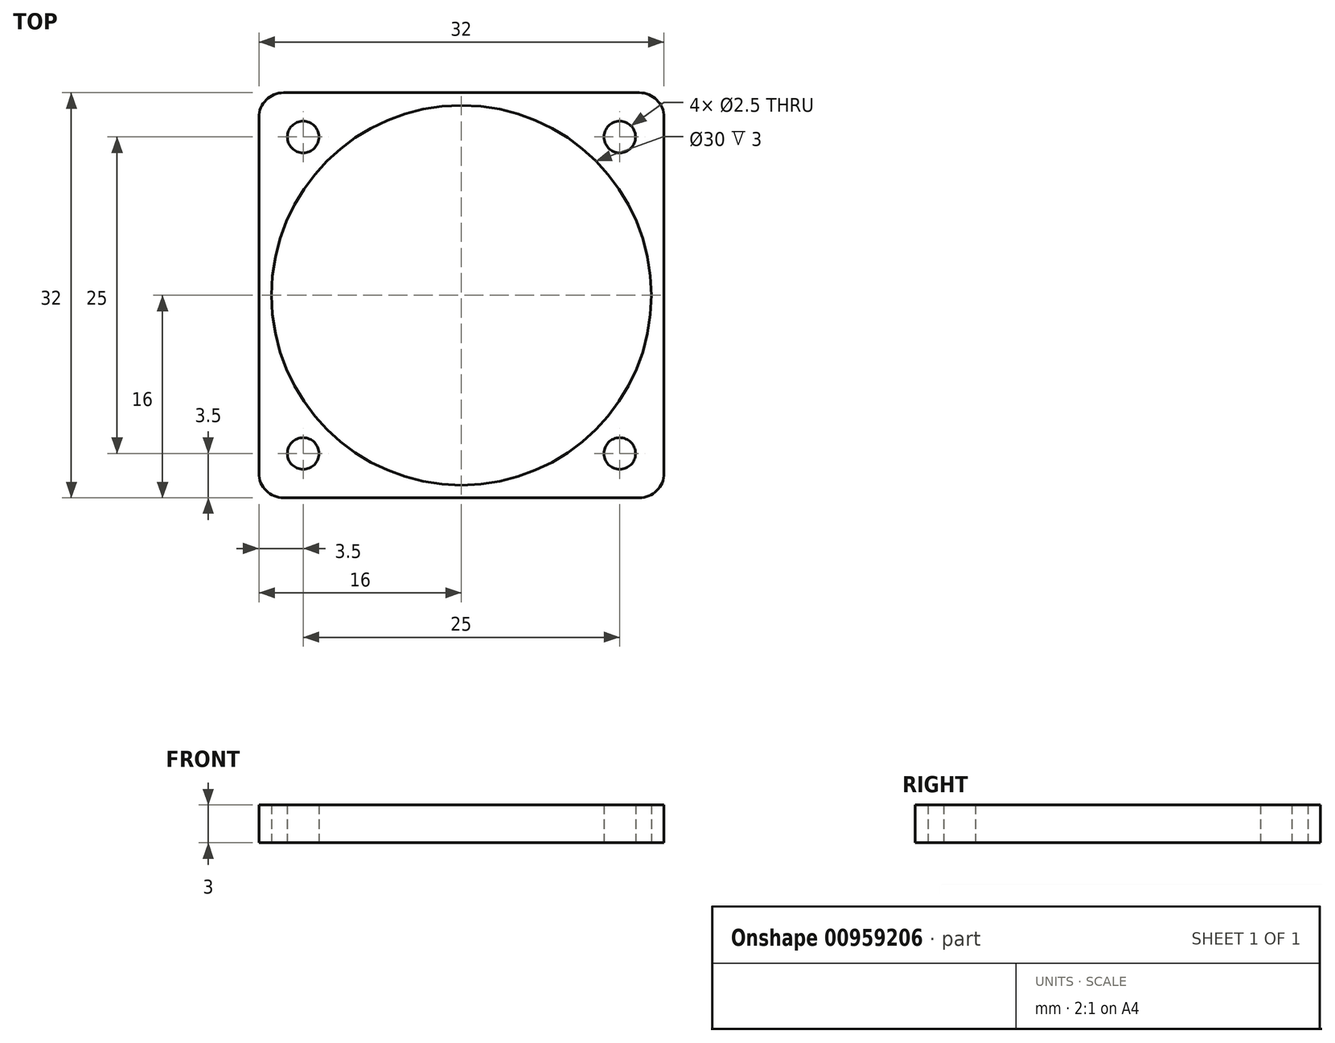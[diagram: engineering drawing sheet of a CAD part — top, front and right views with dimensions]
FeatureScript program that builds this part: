
annotation { "Feature Type Name" : "Feature", "Feature Type Description" : "" }
export const myFeature = defineFeature(function(context is Context, id is Id, definition is map)
    precondition{}
    {
        {
            var Q0;
            Q0=qCreatedBy(makeId("Top.planeOp"),FACE);
            var sketch = newSketch(context, id + "F0", { "sketchPlane" : qUnion([Q0])});
            skCircle(sketch, "E0", {"center": v(0, 0) * mm, "radius": 15 * mm});
            skCircle(sketch, "E1", {"center": v(0, 0) * mm, "radius": 17.68 * mm, "construction": true});
            skLineSegment(sketch, "E2.bottom", {"start": v(16, -16) * mm, "end": v(-16, -16) * mm});
            skLineSegment(sketch, "E2.top", {"start": v(16, 16) * mm, "end": v(-16, 16) * mm});
            skLineSegment(sketch, "E2.left", {"start": v(16, -16) * mm, "end": v(16, 16) * mm});
            skLineSegment(sketch, "E2.right", {"start": v(-16, -16) * mm, "end": v(-16, 16) * mm});
            skLineSegment(sketch, "E3", {"start": v(-16, 16) * mm, "end": v(16, -16) * mm, "construction": true});
            skLineSegment(sketch, "E4", {"start": v(-16, -16) * mm, "end": v(16, 16) * mm, "construction": true});
            skCircle(sketch, "E5", {"center": v(-12.5, 12.5) * mm, "radius": 1.25 * mm});
            skCircle(sketch, "E6", {"center": v(12.5, 12.5) * mm, "radius": 1.25 * mm});
            skCircle(sketch, "E7", {"center": v(-12.5, -12.5) * mm, "radius": 1.25 * mm});
            skCircle(sketch, "E8", {"center": v(12.5, -12.5) * mm, "radius": 1.25 * mm});
            skSolve(sketch);
        }
        {
            var Q0;
            Q0=makeQuery(id+"F0.imprint","IMPRINT",FACE,{"disambiguationData":[TD([[makeQuery(id+"F0.imprint","IMPRINT",EDGE,{"derivedFrom":sQuery(id+"F0.wireOp",EDGE,"E0")}),-1.0]])]});
            extrude(context, id + "F1", {"entities" : qUnion([Q0]), "depth" : 3 * mm, "offsetDistance" : 25 * mm});
        }
        {
            var Q0;
            Q0=makeQuery(id+"F1.opExtrude","SWEPT_EDGE",EDGE,{"disambiguationData":[OSD([sQuery(id+"F0.wireOp",EDGE,"E2.bottom"),sQuery(id+"F0.wireOp",EDGE,"E2.left")])]});
            var Q1;
            Q1=makeQuery(id+"F1.opExtrude","SWEPT_EDGE",EDGE,{"disambiguationData":[OSD([sQuery(id+"F0.wireOp",EDGE,"E2.top"),sQuery(id+"F0.wireOp",EDGE,"E2.left")])]});
            var Q2;
            Q2=makeQuery(id+"F1.opExtrude","SWEPT_EDGE",EDGE,{"disambiguationData":[OSD([sQuery(id+"F0.wireOp",EDGE,"E2.top"),sQuery(id+"F0.wireOp",EDGE,"E2.right")])]});
            var Q3;
            Q3=makeQuery(id+"F1.opExtrude","SWEPT_EDGE",EDGE,{"disambiguationData":[OSD([sQuery(id+"F0.wireOp",EDGE,"E2.bottom"),sQuery(id+"F0.wireOp",EDGE,"E2.right")])]});
            fillet(context, id + "F2", {"entities" : qUnion([Q0, Q1, Q2, Q3]), "radius" : 1.95 * mm, "tangentPropagation" : true, "allowEdgeOverflow" : false});
        }
    });
